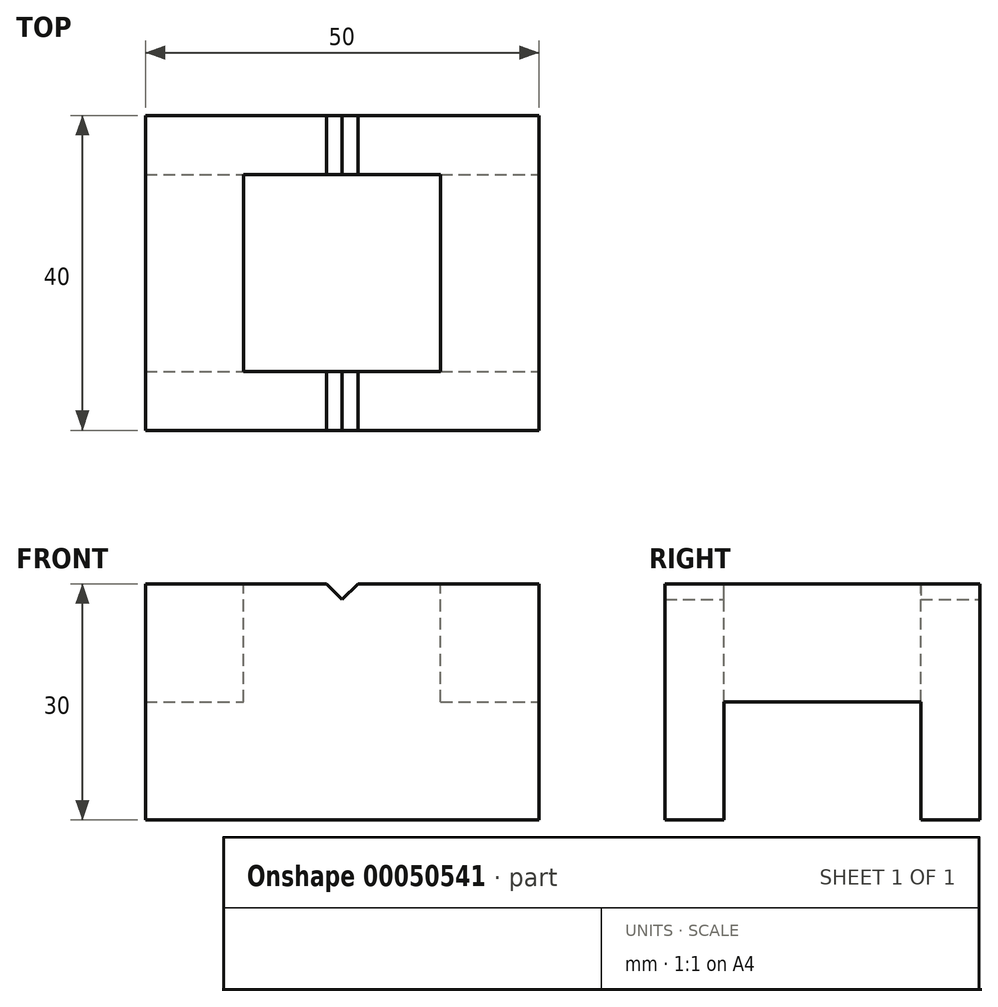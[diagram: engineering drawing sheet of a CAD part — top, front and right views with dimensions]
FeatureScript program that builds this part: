
annotation { "Feature Type Name" : "Feature", "Feature Type Description" : "" }
export const myFeature = defineFeature(function(context is Context, id is Id, definition is map)
    precondition{}
    {
        {
            var Q0;
            Q0=qCreatedBy(makeId("Top.planeOp"),FACE);
            var sketch = newSketch(context, id + "F0", { "sketchPlane" : qUnion([Q0])});
            skLineSegment(sketch, "E0.rect.bottom", {"start": v(-25, 20) * mm, "end": v(25, 20) * mm});
            skLineSegment(sketch, "E0.rect.top", {"start": v(-25, -20) * mm, "end": v(25, -20) * mm});
            skLineSegment(sketch, "E0.rect.left", {"start": v(-25, 20) * mm, "end": v(-25, -20) * mm});
            skLineSegment(sketch, "E0.rect.right", {"start": v(25, 20) * mm, "end": v(25, -20) * mm});
            skPoint(sketch, "E0.rect.middle", {"position": v(0, 0) * mm});
            skSolve(sketch);
        }
        {
            var Q0;
            Q0 = qSketchRegion(id + "F0", true);
            extrude(context, id + "F1", {"entities" : qUnion([Q0]), "depth" : 30 * mm});
        }
        {
            var Q0;
            Q0=makeQuery(id+"F1.opExtrude","SWEPT_FACE",FACE,{"disambiguationData":[OSD([sQuery(id+"F0.wireOp",EDGE,"E0.rect.right")])]});
            var sketch = newSketch(context, id + "F2", { "sketchPlane" : qUnion([Q0])});
            skLineSegment(sketch, "E1.rect.bottom", {"start": v(-12.5, 15) * mm, "end": v(12.5, 15) * mm});
            skLineSegment(sketch, "E1.rect.top", {"start": v(-12.5, -15) * mm, "end": v(12.5, -15) * mm});
            skLineSegment(sketch, "E1.rect.left", {"start": v(-12.5, 15) * mm, "end": v(-12.5, -15) * mm});
            skLineSegment(sketch, "E1.rect.right", {"start": v(12.5, 15) * mm, "end": v(12.5, -15) * mm});
            skPoint(sketch, "E1.rect.middle", {"position": v(0, 0) * mm});
            skSolve(sketch);
        }
        {
            var Q0;
            Q0 = qSketchRegion(id + "F2", true);
            extrude(context, id + "F3", {"entities" : qUnion([Q0]), "operationType" : NewBodyOperationType.REMOVE, "endBound" : BoundingType.THROUGH_ALL, "oppositeDirection" : true, "depth" : 25 * mm});
        }
        {
            var Q0;
            Q0=makeQuery(id+"F1.opExtrude","CAP_FACE",FACE,{"disambiguationData":[OSD([sQuery(id+"F0.wireOp",EDGE,"E0.rect.bottom"),sQuery(id+"F0.wireOp",EDGE,"E0.rect.top"),sQuery(id+"F0.wireOp",EDGE,"E0.rect.left"),sQuery(id+"F0.wireOp",EDGE,"E0.rect.right")])],"isStart":false});
            var sketch = newSketch(context, id + "F4", { "sketchPlane" : qUnion([Q0])});
            skLineSegment(sketch, "E2.rect.bottom", {"start": v(-12.5, -12.5) * mm, "end": v(12.5, -12.5) * mm});
            skLineSegment(sketch, "E2.rect.top", {"start": v(-12.5, 12.5) * mm, "end": v(12.5, 12.5) * mm});
            skLineSegment(sketch, "E2.rect.left", {"start": v(-12.5, -12.5) * mm, "end": v(-12.5, 12.5) * mm});
            skLineSegment(sketch, "E2.rect.right", {"start": v(12.5, -12.5) * mm, "end": v(12.5, 12.5) * mm});
            skPoint(sketch, "E2.rect.middle", {"position": v(0, 0) * mm});
            skSolve(sketch);
        }
        {
            var Q0;
            Q0 = qSketchRegion(id + "F4", true);
            extrude(context, id + "F5", {"entities" : qUnion([Q0]), "operationType" : NewBodyOperationType.REMOVE, "endBound" : BoundingType.THROUGH_ALL, "oppositeDirection" : true, "depth" : 25 * mm});
        }
        {
            var Q0;
            Q0=makeQuery(id+"F1.opExtrude","SWEPT_FACE",FACE,{"disambiguationData":[OSD([sQuery(id+"F0.wireOp",EDGE,"E0.rect.bottom")])]});
            var sketch = newSketch(context, id + "F6", { "sketchPlane" : qUnion([Q0])});
            skLineSegment(sketch, "E3", {"start": v(0, 30) * mm, "end": v(2, 30) * mm});
            skLineSegment(sketch, "E4", {"start": v(2, 30) * mm, "end": v(0, 28) * mm});
            skLineSegment(sketch, "E5", {"start": v(0, 28) * mm, "end": v(-2, 30) * mm});
            skLineSegment(sketch, "E6", {"start": v(-2, 30) * mm, "end": v(0, 30) * mm});
            skSolve(sketch);
        }
        {
            var Q0;
            Q0=makeQuery(id+"F6.imprint","IMPRINT",FACE,{"disambiguationData":[TD([[makeQuery(id+"F6.imprint","IMPRINT",EDGE,{"derivedFrom":sQuery(id+"F6.wireOp",EDGE,"E3")}),1.0]])]});
            extrude(context, id + "F7", {"entities" : qUnion([Q0]), "operationType" : NewBodyOperationType.REMOVE, "endBound" : BoundingType.THROUGH_ALL, "oppositeDirection" : true, "depth" : 25 * mm});
        }
    });
